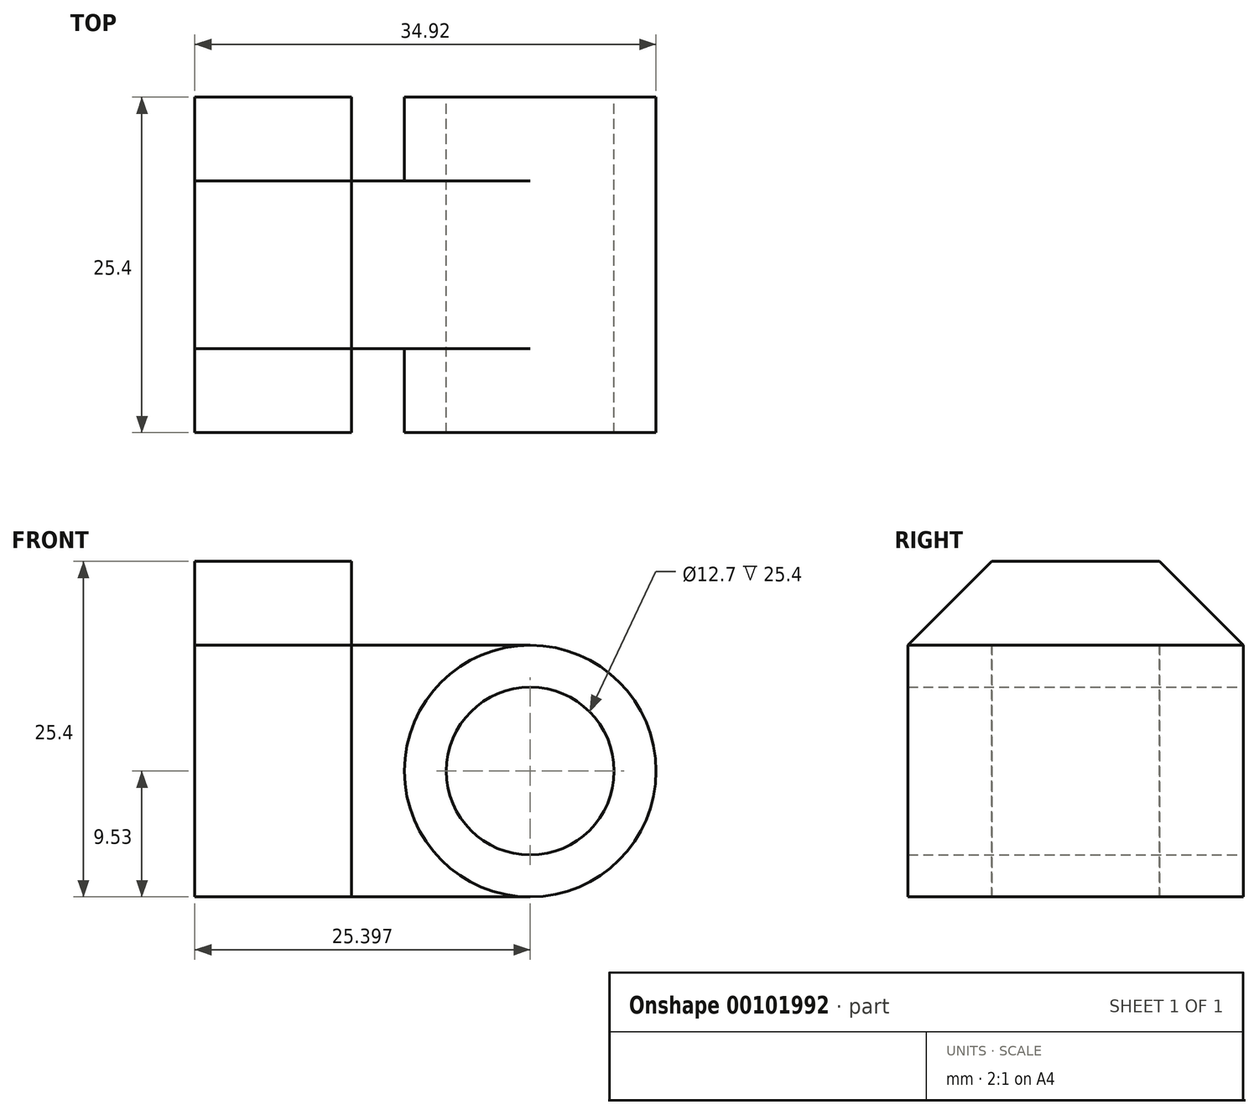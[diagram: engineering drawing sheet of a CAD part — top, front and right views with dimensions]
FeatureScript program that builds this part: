
annotation { "Feature Type Name" : "Feature", "Feature Type Description" : "" }
export const myFeature = defineFeature(function(context is Context, id is Id, definition is map)
    precondition{}
    {
        {
            var Q0;
            Q0=qCreatedBy(makeId("Front.planeOp"),FACE);
            var sketch = newSketch(context, id + "F0", { "sketchPlane" : qUnion([Q0])});
            skLineSegment(sketch, "E0", {"start": v(-41.97, -30.12) * mm, "end": v(-30.1, -30.12) * mm});
            skLineSegment(sketch, "E1", {"start": v(-30.1, -30.12) * mm, "end": v(-30.1, -11.07) * mm});
            skLineSegment(sketch, "E2", {"start": v(-30.1, -11.07) * mm, "end": v(-41.97, -11.07) * mm});
            skLineSegment(sketch, "E3", {"start": v(-41.97, -11.07) * mm, "end": v(-41.97, -30.12) * mm});
            skLineSegment(sketch, "E4", {"start": v(-41.97, -11.07) * mm, "end": v(-41.97, -4.72) * mm});
            skLineSegment(sketch, "E5", {"start": v(-41.97, -4.72) * mm, "end": v(-30.1, -4.72) * mm});
            skLineSegment(sketch, "E6", {"start": v(-30.1, -4.72) * mm, "end": v(-30.1, -11.07) * mm});
            skLineSegment(sketch, "E7", {"start": v(-30.1, -11.07) * mm, "end": v(-16.57, -11.07) * mm});
            skLineSegment(sketch, "E8", {"start": v(-16.57, -11.07) * mm, "end": v(-16.57, -30.12) * mm});
            skLineSegment(sketch, "E9", {"start": v(-16.57, -30.12) * mm, "end": v(-30.1, -30.12) * mm});
            skLineSegment(sketch, "E10", {"start": v(-41.97, -20.6) * mm, "end": v(-16.57, -20.6) * mm, "construction": true});
            skCircle(sketch, "E11", {"center": v(-16.57, -20.6) * mm, "radius": 6.35 * mm});
            skCircle(sketch, "E12", {"center": v(-16.57, -20.6) * mm, "radius": 9.52 * mm});
            skSolve(sketch);
        }
        {
            var Q0;
            Q0=makeQuery(id+"F0.imprint","IMPRINT",FACE,{"disambiguationData":[TD([[makeQuery(id+"F0.imprint","IMPRINT",EDGE,{"derivedFrom":sQuery(id+"F0.wireOp",EDGE,"E0")}),1.0]])]});
            extrude(context, id + "F1", {"entities" : qUnion([Q0]), "depth" : 12.7 * mm, "hasSecondDirection" : true, "secondDirectionOppositeDirection" : true, "secondDirectionDepth" : 12.7 * mm});
        }
        {
            var Q0;
            Q0=makeQuery(id+"F0.imprint","IMPRINT",FACE,{"disambiguationData":[TD([[makeQuery(id+"F0.imprint","IMPRINT",EDGE,{"derivedFrom":sQuery(id+"F0.wireOp",EDGE,"E1")}),-1.0]])]});
            extrude(context, id + "F2", {"entities" : qUnion([Q0]), "operationType" : NewBodyOperationType.ADD, "depth" : 6.35 * mm, "hasSecondDirection" : true, "secondDirectionOppositeDirection" : true, "secondDirectionDepth" : 6.35 * mm});
        }
        {
            var Q0;
            {var subQ1=sQuery(id+"F0.wireOp",EDGE,"E8");var subQ3=sQuery(id+"F0.wireOp",EDGE,"E11");var subQ4=makeQuery(id+"F0.imprint","INTERSECT",VERTEX,{"disambiguationData":[OD(0.0)],"derivedFrom":[subQ1,subQ3]});Q0=makeQuery(id+"F0.imprint","IMPRINT",FACE,{"disambiguationData":[TD([[makeQuery(id+"F0.imprint","IMPRINT",EDGE,{"disambiguationData":[TD([[subQ4,1.0]])],"derivedFrom":subQ3}),-1.0]])]});}
            var Q1;
            {var subQ1=sQuery(id+"F0.wireOp",EDGE,"E8");var subQ3=sQuery(id+"F0.wireOp",EDGE,"E11");var subQ4=makeQuery(id+"F0.imprint","INTERSECT",VERTEX,{"disambiguationData":[OD(0.0)],"derivedFrom":[subQ1,subQ3]});Q1=makeQuery(id+"F0.imprint","IMPRINT",FACE,{"disambiguationData":[TD([[makeQuery(id+"F0.imprint","IMPRINT",EDGE,{"disambiguationData":[TD([[subQ4,-1.0]])],"derivedFrom":subQ3}),-1.0]])]});}
            extrude(context, id + "F3", {"entities" : qUnion([Q0, Q1]), "operationType" : NewBodyOperationType.ADD, "depth" : 12.7 * mm, "hasSecondDirection" : true, "secondDirectionOppositeDirection" : true, "secondDirectionDepth" : 12.7 * mm});
        }
        {
            var Q0;
            Q0=makeQuery(id+"F0.imprint","IMPRINT",FACE,{"disambiguationData":[TD([[makeQuery(id+"F0.imprint","IMPRINT",EDGE,{"derivedFrom":sQuery(id+"F0.wireOp",EDGE,"E2")}),-1.0]])]});
            extrude(context, id + "F4", {"entities" : qUnion([Q0]), "operationType" : NewBodyOperationType.ADD, "depth" : 12.7 * mm, "hasSecondDirection" : true, "secondDirectionOppositeDirection" : true, "secondDirectionDepth" : 12.7 * mm});
        }
        {
            var Q0;
            {var subQ3=sQuery(id+"F0.wireOp",EDGE,"E1");var subQ4=sQuery(id+"F0.wireOp",EDGE,"E2");var subQ7=sQuery(id+"F0.wireOp",EDGE,"E3");var subQ8=sQuery(id+"F0.wireOp",EDGE,"E0");var subQ11=makeQuery(id+"F1.opExtrude","SWEPT_FACE",FACE,{"disambiguationData":[OSD([subQ3])]});Q0=makeQuery(id+"F4.boolean.opBoolean","MERGE",FACE,{"derivedFrom":[makeQuery(id+"F2.boolean.opBoolean","SPLIT",FACE,{"disambiguationData":[TD([makeQuery(id+"F1.opExtrude","CAP_FACE",FACE,{"disambiguationData":[OSD([subQ8,subQ3,subQ4,subQ7])],"isStart":true})])],"derivedFrom":subQ11}),makeQuery(id+"F2.boolean.opBoolean","SPLIT",FACE,{"disambiguationData":[TD([makeQuery(id+"F1.opExtrude","CAP_FACE",FACE,{"disambiguationData":[OSD([subQ8,subQ3,subQ4,subQ7])],"isStart":false})])],"derivedFrom":subQ11}),makeQuery(id+"F4.opExtrude","SWEPT_FACE",FACE,{"disambiguationData":[OSD([sQuery(id+"F0.wireOp",EDGE,"E6")])]})]});}
            var sketch = newSketch(context, id + "F5", { "sketchPlane" : qUnion([Q0])});
            skLineSegment(sketch, "E13", {"start": v(-6.35, -4.72) * mm, "end": v(-12.7, -11.07) * mm});
            skPoint(sketch, "E13.startSnap0", {"position": v(-6.35, -7.9) * mm});
            skLineSegment(sketch, "E14", {"start": v(-12.7, -11.07) * mm, "end": v(-6.35, -11.07) * mm});
            skLineSegment(sketch, "E15", {"start": v(-6.35, -11.07) * mm, "end": v(6.35, -11.07) * mm});
            skLineSegment(sketch, "E16", {"start": v(6.35, -11.07) * mm, "end": v(12.7, -11.07) * mm});
            skLineSegment(sketch, "E17", {"start": v(12.7, -11.07) * mm, "end": v(6.35, -4.72) * mm});
            skLineSegment(sketch, "E18", {"start": v(6.35, -4.72) * mm, "end": v(-6.35, -4.72) * mm});
            skSolve(sketch);
        }
        {
            var Q0;
            {var subQ0=sQuery(id+"F5.wireOp",EDGE,"E17");Q0=makeQuery(id+"F5.imprint","IMPRINT",FACE,{"disambiguationData":[TD([[makeQuery(id+"F5.imprint","IMPRINT",EDGE,{"derivedFrom":subQ0}),-1.0]])]});}
            var Q1;
            {var subQ0=sQuery(id+"F5.wireOp",EDGE,"E13");Q1=makeQuery(id+"F5.imprint","IMPRINT",FACE,{"disambiguationData":[TD([[makeQuery(id+"F5.imprint","IMPRINT",EDGE,{"derivedFrom":subQ0}),-1.0]])]});}
            extrude(context, id + "F6", {"entities" : qUnion([Q0, Q1]), "operationType" : NewBodyOperationType.REMOVE, "oppositeDirection" : true, "depth" : 12.7 * mm});
        }
    });
